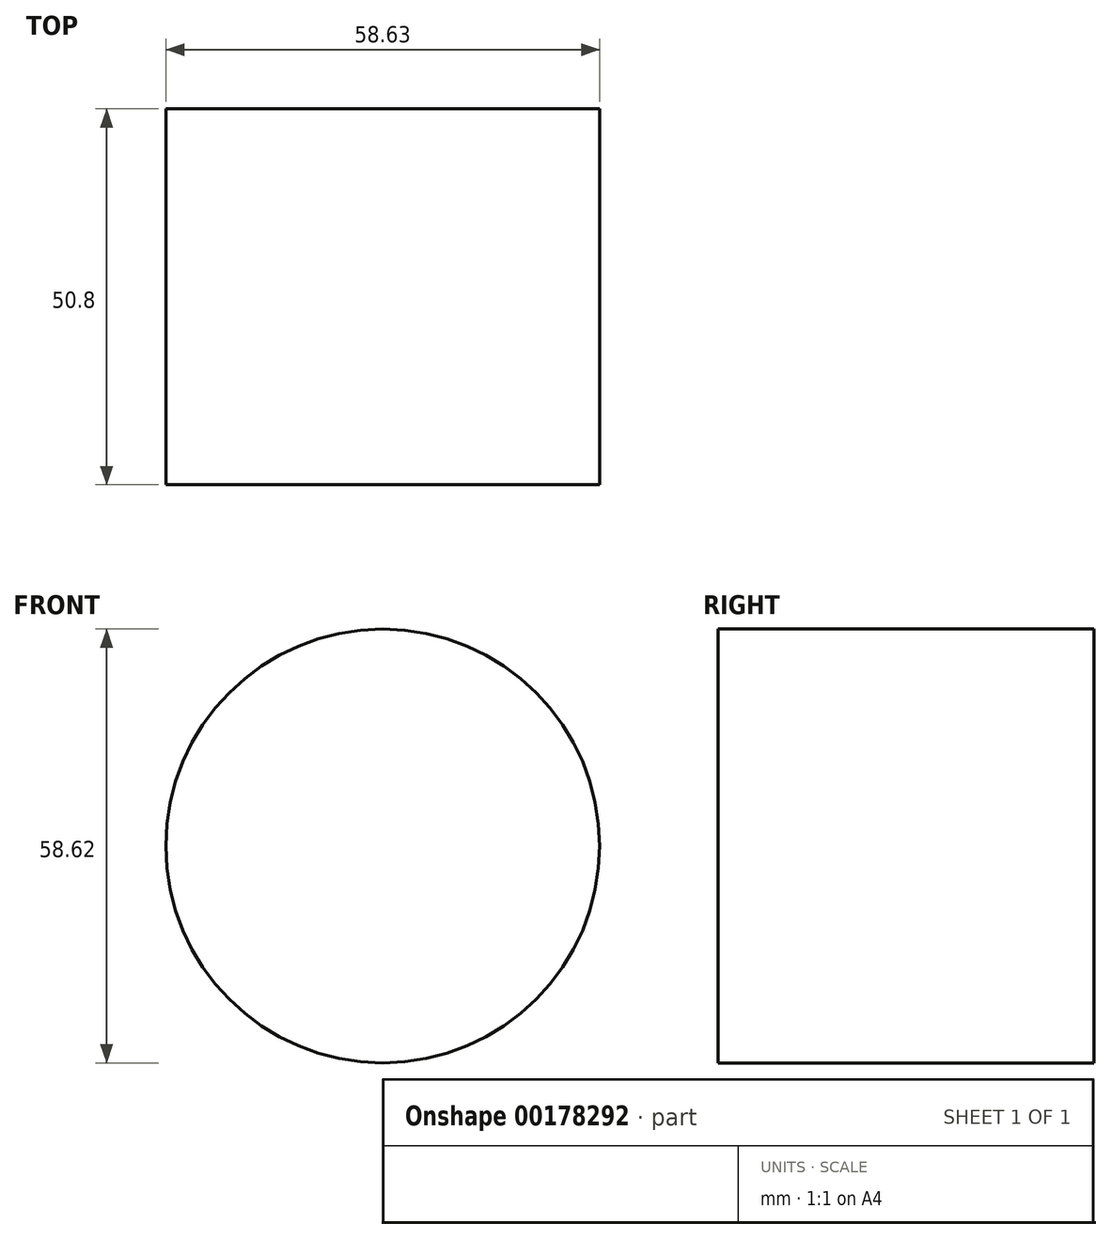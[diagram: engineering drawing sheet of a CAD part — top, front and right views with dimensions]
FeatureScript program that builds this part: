
annotation { "Feature Type Name" : "Feature", "Feature Type Description" : "" }
export const myFeature = defineFeature(function(context is Context, id is Id, definition is map)
    precondition{}
    {
        {
            var Q0;
            Q0=qCreatedBy(makeId("Front.planeOp"),FACE);
            var sketch = newSketch(context, id + "F0", { "sketchPlane" : qUnion([Q0])});
            skCircle(sketch, "E0", {"center": v(-22.25, 16.81) * mm, "radius": 29.31 * mm});
            skSolve(sketch);
        }
        {
            var Q0;
            Q0 = qConstructionFilter(qBodyType(qCreatedBy(id + "F0" ,EDGE), BodyType.WIRE), ConstructionObject.NO);
            extrude(context, id + "F1", {"bodyType" : ToolBodyType.SURFACE, "surfaceEntities" : qUnion([Q0]), "depth" : 50.8 * mm});
        }
    });
